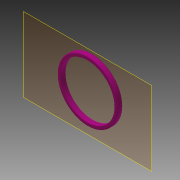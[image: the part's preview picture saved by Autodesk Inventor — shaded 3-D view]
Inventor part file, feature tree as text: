
AUTODESK INVENTOR PART (.ipt)
format: ipt  version: 2014 (Build 180170000, 170)  size: 105,984 bytes
history: native  units: in
note: dims shown in document units (in); Inventor stores cm internally (conversion verified against a paired STEP export)
features: reference x2, plane x1, extrude x1, fillet x1, sketch x1
ambient origin geometry x8: Origin, YZ Plane, XZ Plane, XY Plane, X Axis, Y Axis, Z Axis, Center Point
bodies: Solid1 (feature_tree)
feature tree (6):
  plane  "Work Plane1"
  extrude  "Extrusion1"  Depth=0.15in TaperAngle=0.0deg
  fillet  "Fillet1"  Radius=0.025in
  sketch  "Sketch1"  dims[d0=0.1in d1=0.15in d2=0.0in d3=0.025in]
  reference  "Reference1"
  reference  "Reference2"
